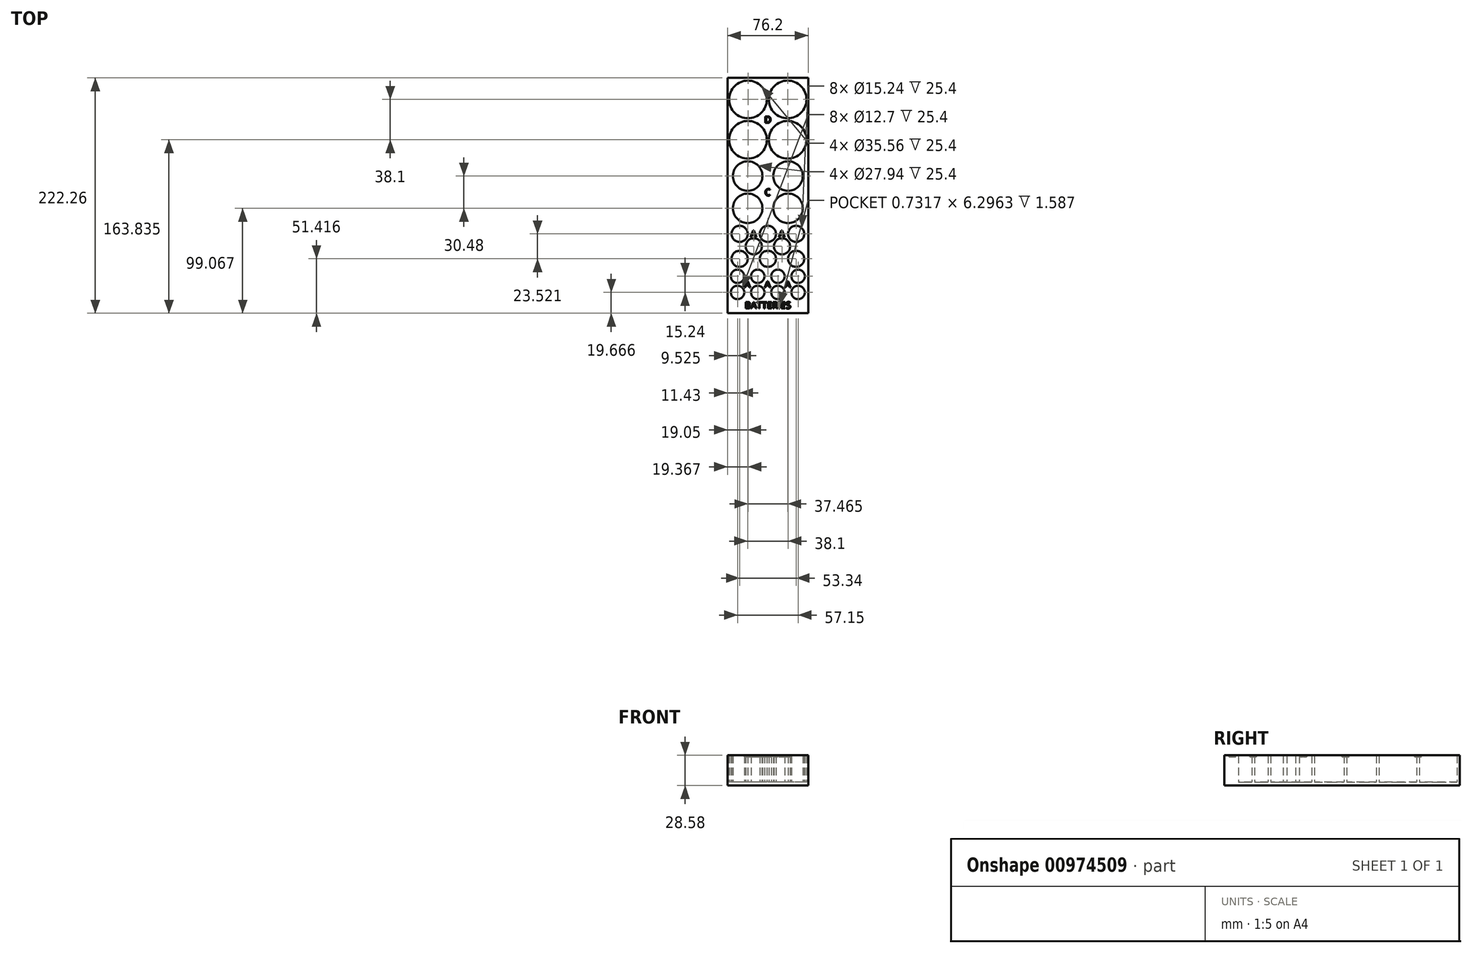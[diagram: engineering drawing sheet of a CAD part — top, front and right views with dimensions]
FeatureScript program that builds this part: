
annotation { "Feature Type Name" : "Feature", "Feature Type Description" : "" }
export const myFeature = defineFeature(function(context is Context, id is Id, definition is map)
    precondition{}
    {
        {
            var Q0;
            Q0=qCreatedBy(makeId("Top.planeOp"),FACE);
            var sketch = newSketch(context, id + "F0", { "sketchPlane" : qUnion([Q0])});
            skLineSegment(sketch, "E0.bottom", {"start": v(38.1, -130.18) * mm, "end": v(-38.1, -130.18) * mm});
            skLineSegment(sketch, "E0.top", {"start": v(38.1, 130.18) * mm, "end": v(-38.1, 130.18) * mm});
            skLineSegment(sketch, "E0.left", {"start": v(38.1, -130.18) * mm, "end": v(38.1, 130.18) * mm});
            skLineSegment(sketch, "E0.right", {"start": v(-38.1, -130.18) * mm, "end": v(-38.1, 130.18) * mm});
            skPoint(sketch, "E0.middle", {"position": v(0, 0) * mm});
            skCircle(sketch, "E1", {"center": v(-18.73, 109.85) * mm, "radius": 17.78 * mm});
            skCircle(sketch, "E2", {"center": v(18.73, 109.86) * mm, "radius": 17.78 * mm});
            skCircle(sketch, "E3", {"center": v(-18.73, 71.75) * mm, "radius": 17.78 * mm});
            skCircle(sketch, "E4", {"center": v(18.73, 71.75) * mm, "radius": 17.78 * mm});
            skCircle(sketch, "E5", {"center": v(-19.05, 37.47) * mm, "radius": 13.97 * mm});
            skCircle(sketch, "E6", {"center": v(19.05, 37.47) * mm, "radius": 13.97 * mm});
            skCircle(sketch, "E7", {"center": v(-19.05, 6.99) * mm, "radius": 13.97 * mm});
            skCircle(sketch, "E8", {"center": v(19.05, 6.99) * mm, "radius": 13.97 * mm});
            skCircle(sketch, "E9", {"center": v(0, -17.14) * mm, "radius": 7.62 * mm});
            skLineSegment(sketch, "E10", {"start": v(-38.1, -6.98) * mm, "end": v(38.1, -6.98) * mm, "construction": true});
            skCircle(sketch, "E11", {"center": v(-26.67, -17.14) * mm, "radius": 7.62 * mm});
            skCircle(sketch, "E12", {"center": v(26.67, -17.14) * mm, "radius": 7.62 * mm});
            skCircle(sketch, "E13", {"center": v(-13.34, -28.9) * mm, "radius": 7.62 * mm});
            skCircle(sketch, "E14", {"center": v(13.34, -28.9) * mm, "radius": 7.62 * mm});
            skCircle(sketch, "E15", {"center": v(-26.67, -40.66) * mm, "radius": 7.62 * mm});
            skCircle(sketch, "E16", {"center": v(0, -40.66) * mm, "radius": 7.62 * mm});
            skCircle(sketch, "E17", {"center": v(26.67, -40.66) * mm, "radius": 7.62 * mm});
            skLineSegment(sketch, "E18", {"start": v(-38.1, -48.28) * mm, "end": v(38.1, -48.28) * mm, "construction": true});
            skCircle(sketch, "E19", {"center": v(-28.57, -57.17) * mm, "radius": 6.35 * mm});
            skCircle(sketch, "E20", {"center": v(-9.53, -57.17) * mm, "radius": 6.35 * mm});
            skCircle(sketch, "E21", {"center": v(9.53, -57.17) * mm, "radius": 6.35 * mm});
            skCircle(sketch, "E22", {"center": v(28.58, -57.17) * mm, "radius": 6.35 * mm});
            skCircle(sketch, "E23", {"center": v(-28.57, -72.41) * mm, "radius": 6.35 * mm});
            skCircle(sketch, "E24", {"center": v(-9.53, -72.41) * mm, "radius": 6.35 * mm});
            skCircle(sketch, "E25", {"center": v(9.53, -72.41) * mm, "radius": 6.35 * mm});
            skCircle(sketch, "E26", {"center": v(28.58, -72.41) * mm, "radius": 6.35 * mm});
            skLineSegment(sketch, "E27", {"start": v(-38.1, -78.76) * mm, "end": v(38.1, -78.76) * mm, "construction": true});
            skLineSegment(sketch, "E28", {"start": v(-38.1, 90.8) * mm, "end": v(38.1, 90.8) * mm, "construction": true});
            skLineSegment(sketch, "E29", {"start": v(-38.1, 22.23) * mm, "end": v(38.1, 22.23) * mm, "construction": true});
            skLineSegment(sketch, "E30", {"start": v(-26.28, -17.14) * mm, "end": v(0, -17.14) * mm, "construction": true});
            skLineSegment(sketch, "E31", {"start": v(-13.34, -28.9) * mm, "end": v(-13.34, -6.98) * mm, "construction": true});
            skLineSegment(sketch, "E32", {"start": v(-28.57, -57.17) * mm, "end": v(-9.53, -57.17) * mm, "construction": true});
            skLineSegment(sketch, "E33", {"start": v(-28.57, -72.41) * mm, "end": v(-9.53, -72.41) * mm, "construction": true});
            skLineSegment(sketch, "E34", {"start": v(-19.05, -72.41) * mm, "end": v(-19.05, -57.17) * mm, "construction": true});
            skLineSegment(sketch, "E35", {"start": v(9.53, -72.41) * mm, "end": v(28.58, -72.41) * mm, "construction": true});
            skLineSegment(sketch, "E36", {"start": v(19.05, -72.41) * mm, "end": v(19.05, -51) * mm, "construction": true});
            skSolve(sketch);
        }
        {
            var Q0;
            Q0 = qSketchRegion(id + "F0", true);
            extrude(context, id + "F1", {"entities" : qUnion([Q0]), "depth" : 25.4 * mm, "offsetDistance" : 25.4 * mm});
        }
        {
            var Q0;
            Q0=makeQuery(id+"F1.opExtrude","CAP_FACE",FACE,{"disambiguationData":[OSD([sQuery(id+"F0.wireOp",EDGE,"E0.bottom"),sQuery(id+"F0.wireOp",EDGE,"E0.top"),sQuery(id+"F0.wireOp",EDGE,"E0.left"),sQuery(id+"F0.wireOp",EDGE,"E0.right"),sQuery(id+"F0.wireOp",EDGE,"E1"),sQuery(id+"F0.wireOp",EDGE,"E2"),sQuery(id+"F0.wireOp",EDGE,"E3"),sQuery(id+"F0.wireOp",EDGE,"E4"),sQuery(id+"F0.wireOp",EDGE,"E5"),sQuery(id+"F0.wireOp",EDGE,"E6"),sQuery(id+"F0.wireOp",EDGE,"E7"),sQuery(id+"F0.wireOp",EDGE,"E8"),sQuery(id+"F0.wireOp",EDGE,"E9"),sQuery(id+"F0.wireOp",EDGE,"E11"),sQuery(id+"F0.wireOp",EDGE,"E12"),sQuery(id+"F0.wireOp",EDGE,"E13"),sQuery(id+"F0.wireOp",EDGE,"E14"),sQuery(id+"F0.wireOp",EDGE,"E15"),sQuery(id+"F0.wireOp",EDGE,"E16"),sQuery(id+"F0.wireOp",EDGE,"E17"),sQuery(id+"F0.wireOp",EDGE,"E19"),sQuery(id+"F0.wireOp",EDGE,"E20"),sQuery(id+"F0.wireOp",EDGE,"E21"),sQuery(id+"F0.wireOp",EDGE,"E22"),sQuery(id+"F0.wireOp",EDGE,"E23"),sQuery(id+"F0.wireOp",EDGE,"E24"),sQuery(id+"F0.wireOp",EDGE,"E25"),sQuery(id+"F0.wireOp",EDGE,"E26")])],"isStart":false});
            var sketch = newSketch(context, id + "F2", { "sketchPlane" : qUnion([Q0])});
            skLineSegment(sketch, "E37.0.0", {"start": v(38.1, -130.18) * mm, "end": v(38.1, 130.18) * mm, "construction": true});
            skLineSegment(sketch, "E37.0.1", {"start": v(38.1, 130.18) * mm, "end": v(-38.1, 130.18) * mm, "construction": true});
            skLineSegment(sketch, "E37.0.2", {"start": v(-38.1, 130.18) * mm, "end": v(-38.1, -130.18) * mm, "construction": true});
            skLineSegment(sketch, "E37.0.3", {"start": v(-38.1, -130.18) * mm, "end": v(38.1, -130.18) * mm, "construction": true});
            skCircle(sketch, "E38.0", {"center": v(-18.73, 71.75) * mm, "radius": 17.78 * mm, "construction": true});
            skCircle(sketch, "E39.0", {"center": v(-18.73, 109.85) * mm, "radius": 17.78 * mm, "construction": true});
            skCircle(sketch, "E40.0", {"center": v(18.73, 109.86) * mm, "radius": 17.78 * mm, "construction": true});
            skCircle(sketch, "E41.0", {"center": v(18.73, 71.75) * mm, "radius": 17.78 * mm, "construction": true});
            skCircle(sketch, "E42.0", {"center": v(-19.05, 37.47) * mm, "radius": 13.97 * mm, "construction": true});
            skCircle(sketch, "E43.0", {"center": v(19.05, 37.47) * mm, "radius": 13.97 * mm, "construction": true});
            skCircle(sketch, "E44.0", {"center": v(-19.05, 6.99) * mm, "radius": 13.97 * mm, "construction": true});
            skCircle(sketch, "E45.0", {"center": v(19.05, 6.99) * mm, "radius": 13.97 * mm, "construction": true});
            skCircle(sketch, "E46.0", {"center": v(-26.67, -17.14) * mm, "radius": 7.62 * mm, "construction": true});
            skCircle(sketch, "E47.0", {"center": v(0, -17.14) * mm, "radius": 7.62 * mm, "construction": true});
            skCircle(sketch, "E48.0", {"center": v(26.67, -17.14) * mm, "radius": 7.62 * mm, "construction": true});
            skCircle(sketch, "E49.0", {"center": v(-28.57, -57.17) * mm, "radius": 6.35 * mm, "construction": true});
            skCircle(sketch, "E50.0", {"center": v(-9.53, -57.17) * mm, "radius": 6.35 * mm, "construction": true});
            skCircle(sketch, "E51.0", {"center": v(9.53, -57.17) * mm, "radius": 6.35 * mm, "construction": true});
            skCircle(sketch, "E52.0", {"center": v(28.58, -57.17) * mm, "radius": 6.35 * mm, "construction": true});
            skCircle(sketch, "E53.0", {"center": v(-9.53, -72.41) * mm, "radius": 6.35 * mm, "construction": true});
            skCircle(sketch, "E54.0", {"center": v(9.53, -72.41) * mm, "radius": 6.35 * mm, "construction": true});
            skCircle(sketch, "E55.0", {"center": v(28.58, -72.41) * mm, "radius": 6.35 * mm, "construction": true});
            skCircle(sketch, "E56.0", {"center": v(-28.57, -72.41) * mm, "radius": 6.35 * mm, "construction": true});
            skText(sketch, "E57", { "text": "D", "fontName": "OpenSans-Regular.ttf"});
            skLineSegment(sketch, "E58", {"start": v(-18.73, 71.75) * mm, "end": v(18.73, 71.75) * mm, "construction": true});
            skLineSegment(sketch, "E59", {"start": v(-18.73, 109.85) * mm, "end": v(18.73, 109.86) * mm, "construction": true});
            skLineSegment(sketch, "E60", {"start": v(0, 71.75) * mm, "end": v(0, 109.85) * mm, "construction": true});
            skLineSegment(sketch, "E61", {"start": v(-19.05, 37.47) * mm, "end": v(19.05, 37.47) * mm, "construction": true});
            skLineSegment(sketch, "E62", {"start": v(-19.05, 6.99) * mm, "end": v(19.05, 6.99) * mm, "construction": true});
            skLineSegment(sketch, "E63", {"start": v(0, 6.99) * mm, "end": v(0, 37.47) * mm, "construction": true});
            skText(sketch, "E64", { "text": "C\n", "fontName": "OpenSans-Regular.ttf"});
            skLineSegment(sketch, "E65", {"start": v(-19.05, -17.14) * mm, "end": v(-7.62, -17.14) * mm, "construction": true});
            skLineSegment(sketch, "E66", {"start": v(-7.62, -17.14) * mm, "end": v(7.62, -17.14) * mm, "construction": true});
            skLineSegment(sketch, "E67", {"start": v(7.62, -17.14) * mm, "end": v(19.05, -17.14) * mm, "construction": true});
            skText(sketch, "E68", { "text": "A", "fontName": "OpenSans-Regular.ttf"});
            skText(sketch, "E69", { "text": "A", "fontName": "OpenSans-Regular.ttf"});
            skLineSegment(sketch, "E70", {"start": v(-22.22, -57.17) * mm, "end": v(-15.88, -57.17) * mm, "construction": true});
            skLineSegment(sketch, "E71", {"start": v(-15.88, -57.17) * mm, "end": v(-3.17, -57.17) * mm, "construction": true});
            skLineSegment(sketch, "E72", {"start": v(-3.17, -57.17) * mm, "end": v(3.17, -57.17) * mm, "construction": true});
            skLineSegment(sketch, "E73", {"start": v(3.17, -57.17) * mm, "end": v(15.88, -57.17) * mm, "construction": true});
            skLineSegment(sketch, "E74", {"start": v(15.88, -57.17) * mm, "end": v(22.23, -57.17) * mm, "construction": true});
            skLineSegment(sketch, "E75", {"start": v(-22.22, -72.41) * mm, "end": v(-15.88, -72.41) * mm, "construction": true});
            skLineSegment(sketch, "E76", {"start": v(-15.88, -72.41) * mm, "end": v(-3.17, -72.41) * mm, "construction": true});
            skLineSegment(sketch, "E77", {"start": v(-3.17, -72.41) * mm, "end": v(3.17, -72.41) * mm, "construction": true});
            skLineSegment(sketch, "E78", {"start": v(3.17, -72.41) * mm, "end": v(15.88, -72.41) * mm, "construction": true});
            skLineSegment(sketch, "E79", {"start": v(15.88, -72.41) * mm, "end": v(22.23, -72.41) * mm, "construction": true});
            skLineSegment(sketch, "E80", {"start": v(-19.05, -57.17) * mm, "end": v(-19.05, -72.41) * mm, "construction": true});
            skLineSegment(sketch, "E81", {"start": v(0, -57.17) * mm, "end": v(0, -72.41) * mm, "construction": true});
            skLineSegment(sketch, "E82", {"start": v(19.05, -57.17) * mm, "end": v(19.05, -72.41) * mm, "construction": true});
            skText(sketch, "E83", { "text": "A", "fontName": "OpenSans-Regular.ttf"});
            skLineSegment(sketch, "E84", {"start": v(19.05, -64.8) * mm, "end": v(-19.05, -64.8) * mm, "construction": true});
            skText(sketch, "E85", { "text": "A", "fontName": "OpenSans-Regular.ttf"});
            skText(sketch, "E86", { "text": "A", "fontName": "OpenSans-Regular.ttf"});
            skLineSegment(sketch, "E87", {"start": v(-38.1, -81.3) * mm, "end": v(38.1, -81.3) * mm, "construction": true});
            skText(sketch, "E88", { "text": "BATTERIES\n", "fontName": "OpenSans-Regular.ttf"});
            skLineSegment(sketch, "E89", {"start": v(0, -81.3) * mm, "end": v(0, -109.5) * mm, "construction": true});
            const initialGuessF2  = {"E57": [-0.00323, 0.08763, 1, 0, 0.00635], "E64": [-0.00294, 0.01905, 1, 0, 0.00635], "E68": [-0.01641, -0.02032, 1, 0, 0.00635], "E69": [0.01026, -0.02032, 1, 0, 0.00635], "E83": [-0.02213, -0.06797, 1, 0, 0.00635], "E85": [-0.00308, -0.06797, 1, 0, 0.00635], "E86": [0.01597, -0.06797, 1, 0, 0.00635], "E88": [-0.02188, -0.08765, 1, 0, 0.00635]};
            skSetInitialGuess(sketch, initialGuessF2);
            skSolve(sketch);
        }
        {
            var Q0;
            Q0 = qSketchRegion(id + "F2", true);
            extrude(context, id + "F3", {"entities" : qUnion([Q0]), "operationType" : NewBodyOperationType.REMOVE, "oppositeDirection" : true, "depth" : 1.59 * mm, "offsetDistance" : 25.4 * mm});
        }
        {
            var Q0;
            {var subQ0=sQuery(id+"F0.wireOp",EDGE,"E16");var subQ1=sQuery(id+"F0.wireOp",EDGE,"E15");var subQ2=sQuery(id+"F0.wireOp",EDGE,"E13");var subQ3=sQuery(id+"F0.wireOp",EDGE,"E12");var subQ4=sQuery(id+"F0.wireOp",EDGE,"E11");var subQ5=sQuery(id+"F0.wireOp",EDGE,"E9");var subQ6=sQuery(id+"F0.wireOp",EDGE,"E8");var subQ7=sQuery(id+"F0.wireOp",EDGE,"E7");var subQ8=sQuery(id+"F0.wireOp",EDGE,"E0.left");var subQ9=sQuery(id+"F0.wireOp",EDGE,"E0.top");var subQ10=sQuery(id+"F0.wireOp",EDGE,"E0.right");var subQ11=sQuery(id+"F0.wireOp",EDGE,"E0.bottom");var subQ12=sQuery(id+"F0.wireOp",EDGE,"E6");var subQ13=sQuery(id+"F0.wireOp",EDGE,"E1");var subQ14=sQuery(id+"F0.wireOp",EDGE,"E2");var subQ15=sQuery(id+"F0.wireOp",EDGE,"E3");var subQ16=sQuery(id+"F0.wireOp",EDGE,"E4");var subQ17=sQuery(id+"F0.wireOp",EDGE,"E5");var subQ18=sQuery(id+"F0.wireOp",EDGE,"E24");var subQ19=sQuery(id+"F0.wireOp",EDGE,"E25");var subQ20=sQuery(id+"F0.wireOp",EDGE,"E14");var subQ21=sQuery(id+"F0.wireOp",EDGE,"E26");var subQ22=sQuery(id+"F0.wireOp",EDGE,"E17");var subQ23=sQuery(id+"F0.wireOp",EDGE,"E19");var subQ24=sQuery(id+"F0.wireOp",EDGE,"E20");var subQ25=sQuery(id+"F0.wireOp",EDGE,"E21");var subQ26=sQuery(id+"F0.wireOp",EDGE,"E22");var subQ27=sQuery(id+"F0.wireOp",EDGE,"E23");Q0=makeQuery(id+"F3.boolean.opBoolean","SPLIT",FACE,{"disambiguationData":[TD([makeQuery(id+"F1.opExtrude","SWEPT_FACE",FACE,{"disambiguationData":[OSD([subQ11])]})])],"derivedFrom":makeQuery(id+"F1.opExtrude","CAP_FACE",FACE,{"disambiguationData":[OSD([subQ11,subQ9,subQ8,subQ10,subQ13,subQ14,subQ15,subQ16,subQ17,subQ12,subQ7,subQ6,subQ5,subQ4,subQ3,subQ2,subQ20,subQ1,subQ0,subQ22,subQ23,subQ24,subQ25,subQ26,subQ27,subQ18,subQ19,subQ21])],"isStart":false})});}
            var sketch = newSketch(context, id + "F4", { "sketchPlane" : qUnion([Q0])});
            skLineSegment(sketch, "E90.0.0", {"start": v(38.1, -130.18) * mm, "end": v(38.1, 130.18) * mm, "construction": true});
            skLineSegment(sketch, "E90.0.1", {"start": v(38.1, 130.18) * mm, "end": v(-38.1, 130.18) * mm, "construction": true});
            skLineSegment(sketch, "E90.0.2", {"start": v(-38.1, 130.18) * mm, "end": v(-38.1, -130.18) * mm, "construction": true});
            skLineSegment(sketch, "E90.0.3", {"start": v(-38.1, -130.18) * mm, "end": v(38.1, -130.18) * mm, "construction": true});
            skLineSegment(sketch, "E91.bottom", {"start": v(-38.1, -130.18) * mm, "end": v(38.1, -130.18) * mm});
            skLineSegment(sketch, "E91.top", {"start": v(-38.1, -92.08) * mm, "end": v(38.1, -92.08) * mm});
            skLineSegment(sketch, "E91.left", {"start": v(-38.1, -130.18) * mm, "end": v(-38.1, -92.08) * mm});
            skLineSegment(sketch, "E91.right", {"start": v(38.1, -130.18) * mm, "end": v(38.1, -92.08) * mm});
            skSolve(sketch);
        }
        {
            var Q0;
            Q0 = qSketchRegion(id + "F4", true);
            extrude(context, id + "F5", {"entities" : qUnion([Q0]), "operationType" : NewBodyOperationType.REMOVE, "endBound" : BoundingType.THROUGH_ALL, "oppositeDirection" : true, "depth" : 25.4 * mm, "offsetDistance" : 25.4 * mm});
        }
        {
            var Q0;
            Q0=makeQuery(id+"F1.opExtrude","CAP_FACE",FACE,{"disambiguationData":[OSD([sQuery(id+"F0.wireOp",EDGE,"E0.bottom"),sQuery(id+"F0.wireOp",EDGE,"E0.top"),sQuery(id+"F0.wireOp",EDGE,"E0.left"),sQuery(id+"F0.wireOp",EDGE,"E0.right"),sQuery(id+"F0.wireOp",EDGE,"E1"),sQuery(id+"F0.wireOp",EDGE,"E2"),sQuery(id+"F0.wireOp",EDGE,"E3"),sQuery(id+"F0.wireOp",EDGE,"E4"),sQuery(id+"F0.wireOp",EDGE,"E5"),sQuery(id+"F0.wireOp",EDGE,"E6"),sQuery(id+"F0.wireOp",EDGE,"E7"),sQuery(id+"F0.wireOp",EDGE,"E8"),sQuery(id+"F0.wireOp",EDGE,"E9"),sQuery(id+"F0.wireOp",EDGE,"E11"),sQuery(id+"F0.wireOp",EDGE,"E12"),sQuery(id+"F0.wireOp",EDGE,"E13"),sQuery(id+"F0.wireOp",EDGE,"E14"),sQuery(id+"F0.wireOp",EDGE,"E15"),sQuery(id+"F0.wireOp",EDGE,"E16"),sQuery(id+"F0.wireOp",EDGE,"E17"),sQuery(id+"F0.wireOp",EDGE,"E19"),sQuery(id+"F0.wireOp",EDGE,"E20"),sQuery(id+"F0.wireOp",EDGE,"E21"),sQuery(id+"F0.wireOp",EDGE,"E22"),sQuery(id+"F0.wireOp",EDGE,"E23"),sQuery(id+"F0.wireOp",EDGE,"E24"),sQuery(id+"F0.wireOp",EDGE,"E25"),sQuery(id+"F0.wireOp",EDGE,"E26")])],"isStart":true});
            var sketch = newSketch(context, id + "F6", { "sketchPlane" : qUnion([Q0])});
            skSolve(sketch);
        }
        {
            var Q0;
            {var subQ15=sQuery(id+"F0.wireOp",EDGE,"E0.top");Q0=makeQuery(id+"F6.imprint","IMPRINT",FACE,{"disambiguationData":[TD([[makeQuery(id+"F6.imprint","IMPRINT",EDGE,{"derivedFrom":makeQuery(id+"F1.opExtrude","CAP_EDGE",EDGE,{"disambiguationData":[OSD([subQ15])],"isStart":true})}),-1.0]])]});}
            var sketch = newSketch(context, id + "F7", { "sketchPlane" : qUnion([Q0])});
            skLineSegment(sketch, "E92.0.0", {"start": v(38.1, 92.08) * mm, "end": v(-38.1, 92.08) * mm});
            skLineSegment(sketch, "E92.0.1", {"start": v(-38.1, 92.08) * mm, "end": v(-38.1, -130.18) * mm});
            skLineSegment(sketch, "E92.0.2", {"start": v(-38.1, -130.18) * mm, "end": v(38.1, -130.18) * mm});
            skLineSegment(sketch, "E92.0.3", {"start": v(38.1, -130.18) * mm, "end": v(38.1, 92.08) * mm});
            skSolve(sketch);
        }
        {
            var Q0;
            Q0 = qSketchRegion(id + "F7", true);
            extrude(context, id + "F8", {"entities" : qUnion([Q0]), "operationType" : NewBodyOperationType.ADD, "depth" : 3.17 * mm, "offsetDistance" : 25.4 * mm});
        }
    });
